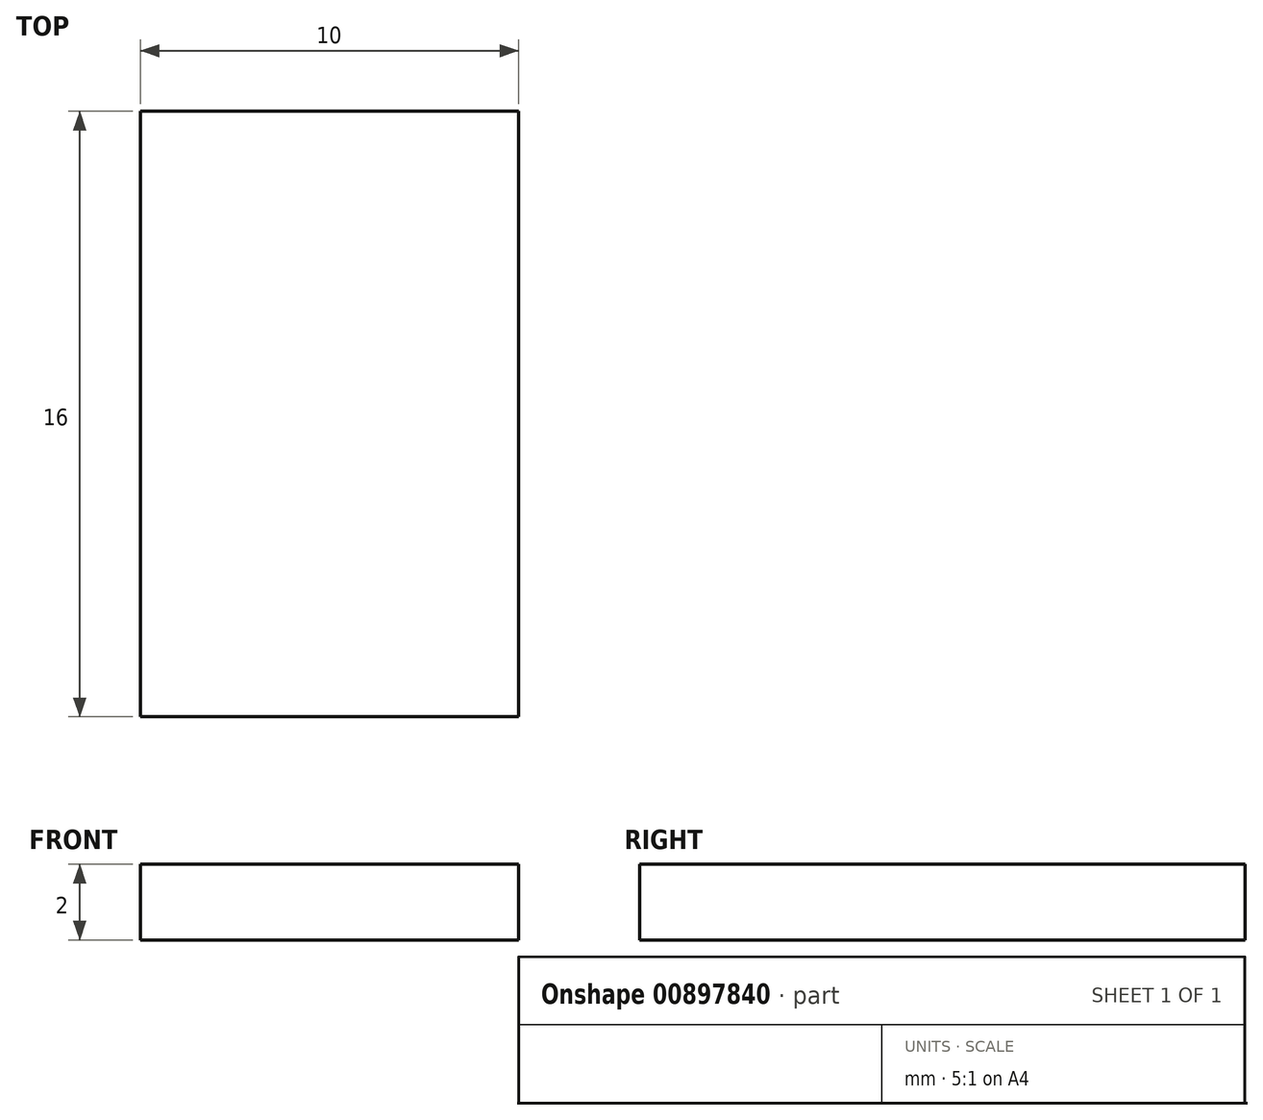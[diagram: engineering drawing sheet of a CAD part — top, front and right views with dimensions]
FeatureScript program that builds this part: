
annotation { "Feature Type Name" : "Feature", "Feature Type Description" : "" }
export const myFeature = defineFeature(function(context is Context, id is Id, definition is map)
    precondition{}
    {
        {
            var Q0;
            Q0=qCreatedBy(makeId("Top.planeOp"),FACE);
            var sketch = newSketch(context, id + "F0", { "sketchPlane" : qUnion([Q0])});
            skLineSegment(sketch, "E0.bottom", {"start": v(5, 8) * mm, "end": v(-5, 8) * mm});
            skLineSegment(sketch, "E0.top", {"start": v(5, -8) * mm, "end": v(-5, -8) * mm});
            skLineSegment(sketch, "E0.left", {"start": v(5, 8) * mm, "end": v(5, -8) * mm});
            skLineSegment(sketch, "E0.right", {"start": v(-5, 8) * mm, "end": v(-5, -8) * mm});
            skPoint(sketch, "E0.middle", {"position": v(0, 0) * mm});
            skSolve(sketch);
        }
        {
            var Q0;
            Q0=makeQuery(id+"F0.imprint","IMPRINT",FACE,{"disambiguationData":[TD([[makeQuery(id+"F0.imprint","IMPRINT",EDGE,{"derivedFrom":sQuery(id+"F0.wireOp",EDGE,"E0.bottom")}),1.0]])]});
            var Q1;
            Q1 = qSketchRegion(id + "F0", true);
            extrude(context, id + "F1", {"entities" : qUnion([Q0, Q1]), "depth" : 2 * mm, "offsetDistance" : 25 * mm});
        }
    });
